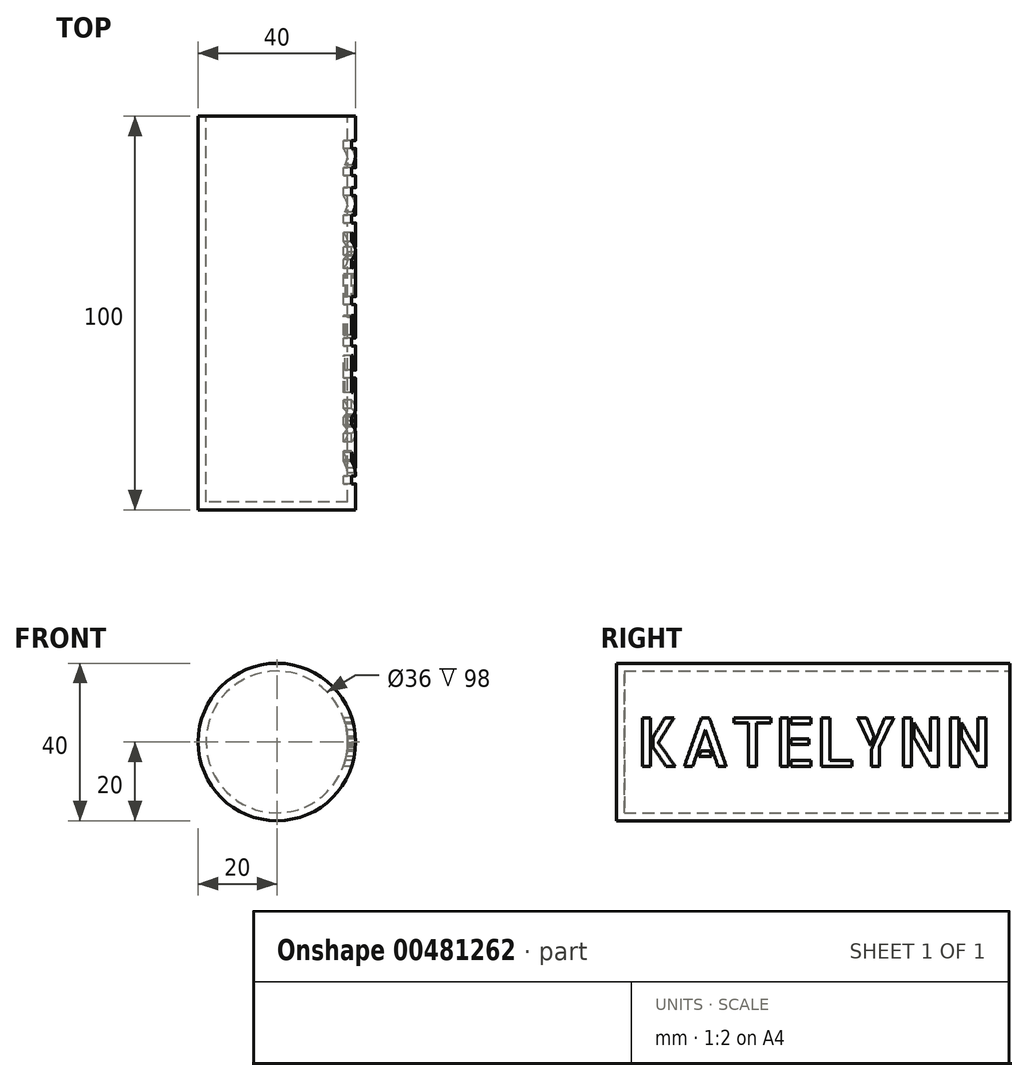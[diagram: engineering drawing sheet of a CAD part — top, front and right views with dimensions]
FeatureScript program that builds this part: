
annotation { "Feature Type Name" : "Feature", "Feature Type Description" : "" }
export const myFeature = defineFeature(function(context is Context, id is Id, definition is map)
    precondition{}
    {
        {
            var Q0;
            Q0=qCreatedBy(makeId("Front.planeOp"),FACE);
            var sketch = newSketch(context, id + "F0", { "sketchPlane" : qUnion([Q0])});
            skLineSegment(sketch, "E0", {"start": v(-20, 100) * mm, "end": v(-20, 0) * mm});
            skLineSegment(sketch, "E1", {"start": v(-20, 0) * mm, "end": v(0, 0) * mm});
            skLineSegment(sketch, "E2", {"start": v(0, 0) * mm, "end": v(0, 2) * mm});
            skLineSegment(sketch, "E3", {"start": v(0, 2) * mm, "end": v(-18, 2) * mm});
            skLineSegment(sketch, "E4", {"start": v(-18, 2) * mm, "end": v(-18, 100) * mm});
            skLineSegment(sketch, "E5", {"start": v(-18, 100) * mm, "end": v(-20, 100) * mm});
            skLineSegment(sketch, "E6", {"start": v(0, 34.72) * mm, "end": v(0, -3.19) * mm, "construction": true});
            skLineSegment(sketch, "E7", {"start": v(-47.72, 0) * mm, "end": v(30.1, 0) * mm, "construction": true});
            skSolve(sketch);
        }
        {
            var Q0;
            Q0 = qSketchRegion(id + "F0", true);
            var Q1;
            Q1=sQuery(id+"F0.wireOp",EDGE,"E6");
            revolve(context, id + "F1", {"entities" : qUnion([Q0]), "axis" : qUnion([Q1]), "revolveType" : RevolveType.FULL});
        }
        {
            var Q0;
            Q0=makeQuery(id+"F1.opRevolve","SWEPT_BODY",BODY,{"disambiguationData":[OSD([sQuery(id+"F0.wireOp",EDGE,"E0"),sQuery(id+"F0.wireOp",EDGE,"E1"),sQuery(id+"F0.wireOp",EDGE,"E2"),sQuery(id+"F0.wireOp",EDGE,"E3"),sQuery(id+"F0.wireOp",EDGE,"E4"),sQuery(id+"F0.wireOp",EDGE,"E5")])]});
            var Q1;
            Q1=sQuery(id+"F0.wireOp",EDGE,"E7");
            transform(context, id + "F2", {"entities" : qUnion([Q0]), "transformType" : TransformType.ROTATION, "transformAxis" : qUnion([Q1]), "angle" : 270 * degree, "makeCopy" : false});
        }
        {
            var Q0;
            Q0=qCreatedBy(makeId("Right.planeOp"),FACE);
            var sketch = newSketch(context, id + "F3", { "sketchPlane" : qUnion([Q0])});
            skText(sketch, "E8", { "text": "KATELYNN", "fontName": "AllertaStencil-Regular.ttf"});
            skLineSegment(sketch, "E9", {"start": v(100, -20) * mm, "end": v(0, -20) * mm, "construction": true});
            skLineSegment(sketch, "E10", {"start": v(0, 20) * mm, "end": v(100, 20) * mm, "construction": true});
            skLineSegment(sketch, "E11.0", {"start": v(100, 20) * mm, "end": v(100, -20) * mm, "construction": true});
            skLineSegment(sketch, "E12.0", {"start": v(0, 20) * mm, "end": v(0, -20) * mm, "construction": true});
            skLineSegment(sketch, "E13", {"start": v(-14.23, 0) * mm, "end": v(76.67, 0) * mm, "construction": true});
            const initialGuessF3  = {"E8": [0.005, -0.00618, 1, 0, 0.01236]};
            skSetInitialGuess(sketch, initialGuessF3);
            skSolve(sketch);
        }
        {
            var Q0;
            Q0 = qSketchRegion(id + "F3", true);
            extrude(context, id + "F4", {"entities" : qUnion([Q0]), "operationType" : NewBodyOperationType.REMOVE, "endBound" : BoundingType.THROUGH_ALL, "depth" : 100 * mm});
        }
    });
